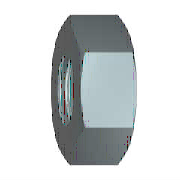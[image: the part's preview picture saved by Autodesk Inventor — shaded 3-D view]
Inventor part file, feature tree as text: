
AUTODESK INVENTOR PART (.ipt)
format: ipt  version: 2023.1 (Build 271208000, 208)  size: 173,056 bytes
history: native  units: mm (DEFAULTED — no unit token found)
features: sketch x3, chamfer x1, hole x1, other x1, plane x1
ambient origin geometry x7: Origin, YZ Plane, XZ Plane, X Axis, Y Axis, Z Axis, Center Point
bodies: Solid1 (feature_tree), Body (feature_tree)
feature tree (7):
  chamfer  "Chamfer1"  Angle=30.0deg  [1 undecoded]
  hole  "Thread"  [1 undecoded]
  other  "Work Axis1"
  plane  "Work Plane1"
  sketch  "Sketch1"  dims[d0=27.712813mm]
  sketch  "Sketch2"  dims[d1=16.4mm]
  sketch  "Sketch3"  dims[d2=0.0mm d3=30.0deg d4=30.0deg d5=24.0mm d6=24.0mm d7=90.0deg d25=13.835mm d26=6.0mm d27=4.0mm d28=2.0mm d29=14.3117mm d30=8.0mm d31=20.594885mm d8=1.082532mm d9=30.0deg d10=1.082532mm d11=30.0deg d13=0.0mm d14=0.0mm d39=0.0mm d40=1.082532mm d41=1.082532mm d42=0.0mm]
note: 2 required parameter values undecoded (feature->parameter linkage not recoverable at this tier; creation-order binding heuristic only, values carry confidence <= 0.55)
